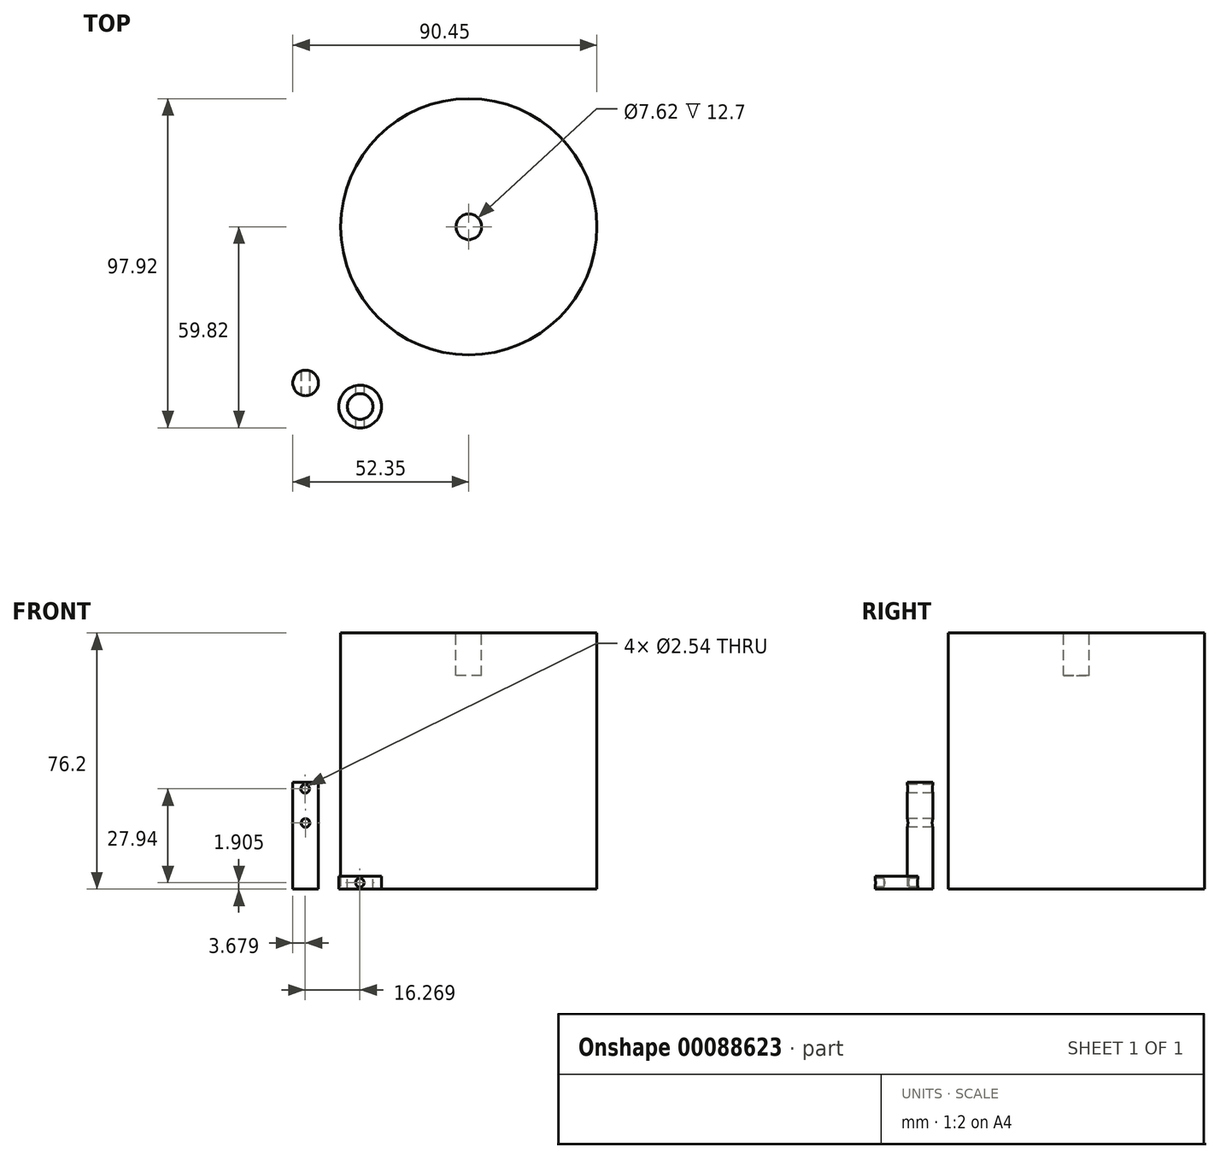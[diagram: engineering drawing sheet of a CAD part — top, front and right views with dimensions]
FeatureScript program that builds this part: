
annotation { "Feature Type Name" : "Feature", "Feature Type Description" : "" }
export const myFeature = defineFeature(function(context is Context, id is Id, definition is map)
    precondition{}
    {
        {
            var Q0;
            Q0=qCreatedBy(makeId("Top.planeOp"),FACE);
            var sketch = newSketch(context, id + "F0", { "sketchPlane" : qUnion([Q0])});
            skCircle(sketch, "E0", {"center": v(0, 0) * mm, "radius": 38.1 * mm});
            skSolve(sketch);
        }
        {
            var Q0;
            Q0 = qSketchRegion(id + "F0", true);
            extrude(context, id + "F1", {"entities" : qUnion([Q0]), "depth" : 76.2 * mm});
        }
        {
            var Q0;
            Q0=makeQuery(id+"F1.opExtrude","CAP_FACE",FACE,{"disambiguationData":[OSD([sQuery(id+"F0.wireOp",EDGE,"E0")])],"isStart":false});
            var sketch = newSketch(context, id + "F2", { "sketchPlane" : qUnion([Q0])});
            skCircle(sketch, "E1", {"center": v(0, 0) * mm, "radius": 3.81 * mm});
            skSolve(sketch);
        }
        {
            var Q0;
            Q0 = qSketchRegion(id + "F2", true);
            extrude(context, id + "F3", {"entities" : qUnion([Q0]), "operationType" : NewBodyOperationType.REMOVE, "oppositeDirection" : true, "depth" : 12.7 * mm});
        }
        {
            var Q0;
            Q0=qCreatedBy(makeId("Top.planeOp"),FACE);
            var sketch = newSketch(context, id + "F4", { "sketchPlane" : qUnion([Q0])});
            skCircle(sketch, "E2", {"center": v(-48.54, -46.46) * mm, "radius": 3.81 * mm});
            skSolve(sketch);
        }
        {
            var Q0;
            Q0 = qSketchRegion(id + "F4", true);
            extrude(context, id + "F5", {"entities" : qUnion([Q0]), "depth" : 31.75 * mm});
        }
        {
            var Q0;
            Q0=qCreatedBy(makeId("Top.planeOp"),FACE);
            var sketch = newSketch(context, id + "F6", { "sketchPlane" : qUnion([Q0])});
            skCircle(sketch, "E3", {"center": v(-32.3, -53.47) * mm, "radius": 6.35 * mm});
            skSolve(sketch);
        }
        {
            var Q0;
            Q0 = qSketchRegion(id + "F6", true);
            extrude(context, id + "F7", {"entities" : qUnion([Q0]), "depth" : 3.8 * mm});
        }
        {
            var Q0;
            Q0=makeQuery(id+"F7.opExtrude","CAP_FACE",FACE,{"disambiguationData":[OSD([sQuery(id+"F6.wireOp",EDGE,"E3")])],"isStart":false});
            var sketch = newSketch(context, id + "F8", { "sketchPlane" : qUnion([Q0])});
            skCircle(sketch, "E4", {"center": v(-32.3, -53.47) * mm, "radius": 3.81 * mm});
            skSolve(sketch);
        }
        {
            var Q0;
            Q0 = qSketchRegion(id + "F8", true);
            extrude(context, id + "F9", {"entities" : qUnion([Q0]), "operationType" : NewBodyOperationType.REMOVE, "oppositeDirection" : true, "depth" : 5.08 * mm});
        }
        {
            var Q0;
            Q0=qCreatedBy(makeId("Front.planeOp"),FACE);
            cPlane(context, id + "F10", {"entities" : qUnion([Q0]), "cplaneType" : CPlaneType.OFFSET, "offset" : 76.2 * mm, "width" : 152.4 * mm, "height" : 152.4 * mm});
        }
        {
            var Q0;
            Q0=qCreatedBy(id+"F10.planeOp",FACE);
            var sketch = newSketch(context, id + "F11", { "sketchPlane" : qUnion([Q0])});
            skCircle(sketch, "E5", {"center": v(-32.4, 1.9) * mm, "radius": 1.27 * mm});
            skSolve(sketch);
        }
        {
            var Q0;
            Q0 = qSketchRegion(id + "F11", true);
            extrude(context, id + "F12", {"entities" : qUnion([Q0]), "operationType" : NewBodyOperationType.REMOVE, "oppositeDirection" : true, "depth" : 38.1 * mm});
        }
        {
            var Q0;
            Q0=qCreatedBy(id+"F10.planeOp",FACE);
            var sketch = newSketch(context, id + "F13", { "sketchPlane" : qUnion([Q0])});
            skCircle(sketch, "E6", {"center": v(-48.67, 29.84) * mm, "radius": 1.27 * mm});
            skSolve(sketch);
        }
        {
            var Q0;
            Q0=qCreatedBy(id+"F10.planeOp",FACE);
            var sketch = newSketch(context, id + "F14", { "sketchPlane" : qUnion([Q0])});
            skCircle(sketch, "E7", {"center": v(-48.57, 19.69) * mm, "radius": 1.27 * mm});
            skSolve(sketch);
        }
        {
            var Q0;
            Q0 = qSketchRegion(id + "F13", true);
            extrude(context, id + "F15", {"entities" : qUnion([Q0]), "operationType" : NewBodyOperationType.REMOVE, "oppositeDirection" : true, "depth" : 38.1 * mm});
        }
        {
            var Q0;
            Q0 = qSketchRegion(id + "F14", true);
            extrude(context, id + "F16", {"entities" : qUnion([Q0]), "operationType" : NewBodyOperationType.REMOVE, "oppositeDirection" : true, "depth" : 38.1 * mm});
        }
    });
